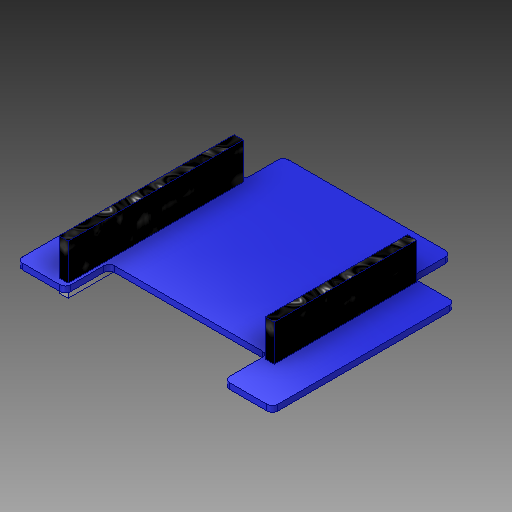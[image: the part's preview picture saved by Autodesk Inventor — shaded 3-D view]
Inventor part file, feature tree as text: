
AUTODESK INVENTOR PART (.ipt)
format: ipt  version: 2019 (Build 230136000, 136)  size: 200,192 bytes
history: native  units: mm
features: extrude x4, sketch x4, other x1, fillet x1
ambient origin geometry x8: Origin, YZ Plane, XZ Plane, XY Plane, X Axis, Y Axis, Z Axis, Center Point
bodies: Solide1 (feature_tree)
feature tree (10):
  other  "X-Nucleo-IKS01A1"
  extrude  "Extrusion1"  Depth=70.0mm
  extrude  "Extrusion2"  Depth=35.0mm
  fillet  "Congé1"  Radius=61.0mm
  extrude  "Extrusion3"  Depth=30.5mm
  extrude  "Extrusion4"  Depth=1.6mm TaperAngle=0.0deg
  sketch  "Esquisse1"
  sketch  "Esquisse2"
  sketch  "Esquisse3"
  sketch  "Esquisse4"
